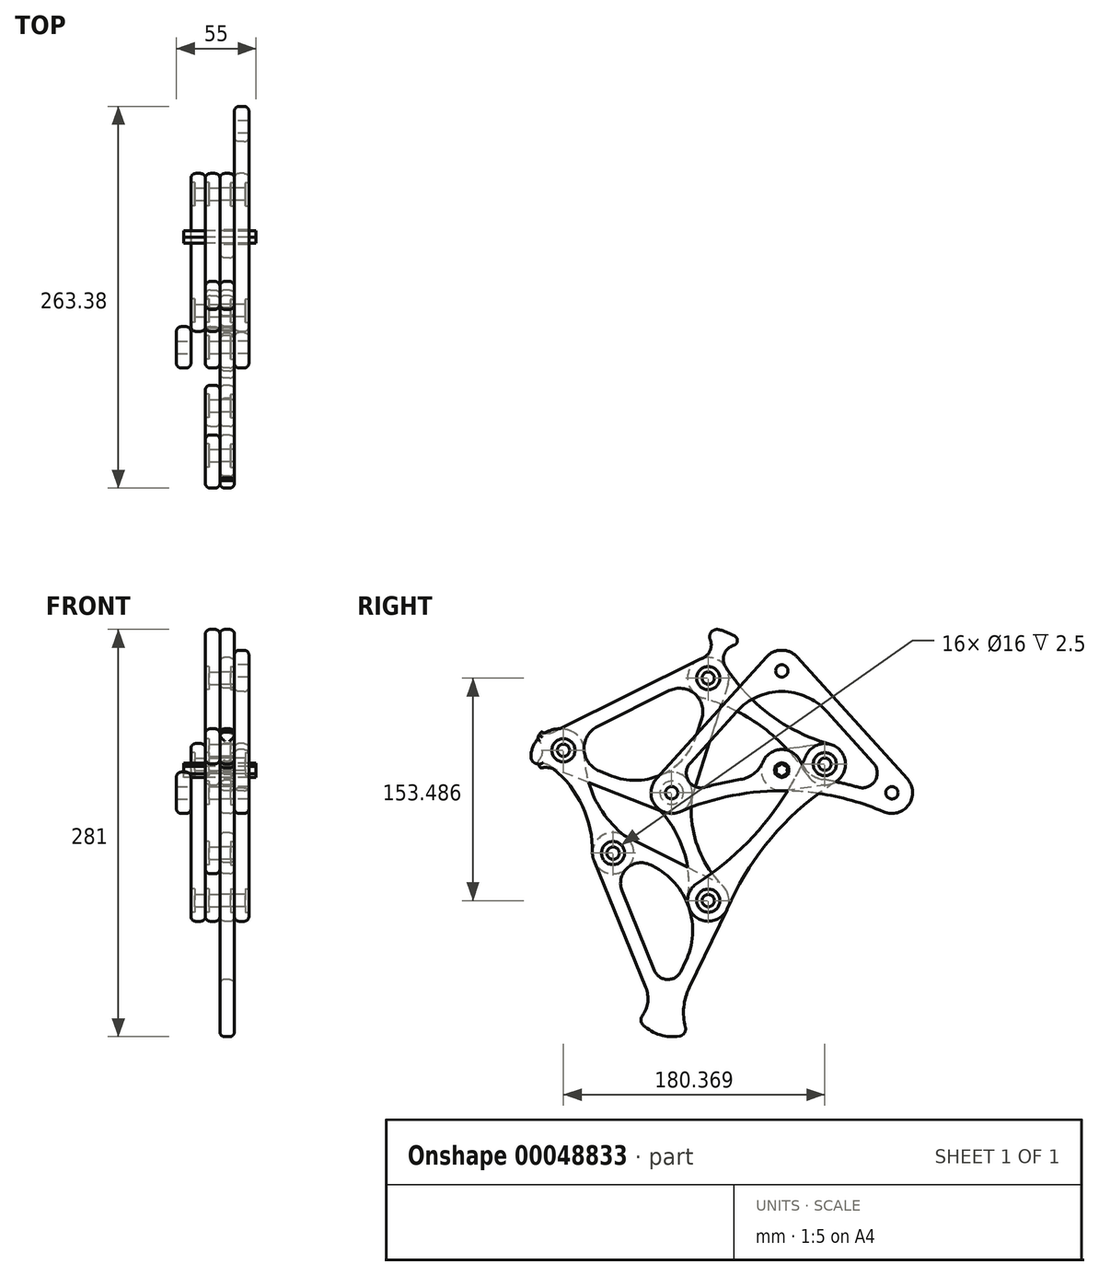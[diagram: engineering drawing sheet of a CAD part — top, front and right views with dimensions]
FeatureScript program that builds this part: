
annotation { "Feature Type Name" : "Feature", "Feature Type Description" : "" }
export const myFeature = defineFeature(function(context is Context, id is Id, definition is map)
    precondition{}
    {
        {
            assignVariable(context, id + "F0", {"name" : "WALL", "anyValue" : 10});
        }
        {
            var Q0;
            Q0=qCreatedBy(makeId("Right.planeOp"),FACE);
            var sketch = newSketch(context, id + "F1", { "sketchPlane" : qUnion([Q0])});
            skLineSegment(sketch, "E0", {"start": v(0, 0) * mm, "end": v(29.72, 4.1) * mm});
            skLineSegment(sketch, "E1", {"start": v(29.72, 4.1) * mm, "end": v(-50.75, 63.47) * mm});
            skLineSegment(sketch, "E2", {"start": v(-50.75, 63.47) * mm, "end": v(-76, -15.6) * mm});
            skLineSegment(sketch, "E3", {"start": v(-76, -15.6) * mm, "end": v(-50.7, -90.02) * mm});
            skLineSegment(sketch, "E4", {"start": v(-50.7, -90.02) * mm, "end": v(29.72, 4.1) * mm});
            skLineSegment(sketch, "E5", {"start": v(-76, -15.6) * mm, "end": v(-150.65, 13.72) * mm});
            skLineSegment(sketch, "E6", {"start": v(-150.65, 13.72) * mm, "end": v(-50.75, 63.47) * mm});
            skLineSegment(sketch, "E7", {"start": v(-50.7, -90.02) * mm, "end": v(-116.38, -57.24) * mm});
            skLineSegment(sketch, "E8", {"start": v(-116.38, -57.24) * mm, "end": v(-150.65, 13.72) * mm});
            skLineSegment(sketch, "E9", {"start": v(-116.38, -57.24) * mm, "end": v(-80.05, -183.52) * mm});
            skLineSegment(sketch, "E10", {"start": v(-80.05, -183.52) * mm, "end": v(-50.7, -90.02) * mm});
            skLineSegment(sketch, "E11", {"start": v(0, 0) * mm, "end": v(0, 67.08) * mm, "construction": true});
            skSolve(sketch);
        }
        {
            var Q0;
            Q0=qCreatedBy(makeId("Right.planeOp"),FACE);
            var sketch = newSketch(context, id + "F2", { "sketchPlane" : qUnion([Q0])});
            skLineSegment(sketch, "E12.rect.bottom", {"start": v(-228.6, 228.6) * mm, "end": v(228.6, 228.6) * mm, "construction": true});
            skLineSegment(sketch, "E12.rect.top", {"start": v(-228.6, -228.6) * mm, "end": v(228.6, -228.6) * mm, "construction": true});
            skLineSegment(sketch, "E12.rect.left", {"start": v(-228.6, 228.6) * mm, "end": v(-228.6, -228.6) * mm, "construction": true});
            skLineSegment(sketch, "E12.rect.right", {"start": v(228.6, 228.6) * mm, "end": v(228.6, -228.6) * mm, "construction": true});
            skPoint(sketch, "E12.rect.middle", {"position": v(0, 0) * mm});
            skSolve(sketch);
        }
        {
            var Q0;
            Q0=qCreatedBy(makeId("Right.planeOp"),FACE);
            var sketch = newSketch(context, id + "F3", { "sketchPlane" : qUnion([Q0])});
            skCircle(sketch, "E13.cCircle", {"center": v(0, 0) * mm, "radius": 6 * mm, "construction": true});
            skLineSegment(sketch, "E13.0", {"start": v(0, 6) * mm, "end": v(5.2, 3) * mm, "construction": true});
            skLineSegment(sketch, "E13.1", {"start": v(5.2, 3) * mm, "end": v(5.2, -3) * mm, "construction": true});
            skLineSegment(sketch, "E13.2", {"start": v(5.2, -3) * mm, "end": v(0, -6) * mm, "construction": true});
            skLineSegment(sketch, "E13.3", {"start": v(0, -6) * mm, "end": v(-5.2, -3) * mm, "construction": true});
            skLineSegment(sketch, "E13.4", {"start": v(-5.2, -3) * mm, "end": v(-5.2, 3) * mm, "construction": true});
            skLineSegment(sketch, "E13.5", {"start": v(-5.2, 3) * mm, "end": v(0, 6) * mm, "construction": true});
            skArc(sketch, "E14", {"start": v(-5.2, 3) * mm, "mid": v(-2.1, 3.63) * mm, "end": v(0, 6) * mm});
            skArc(sketch, "E15.1.0", {"start": v(-5.2, -3) * mm, "mid": v(-4.2, 0) * mm, "end": v(-5.2, 3) * mm});
            skArc(sketch, "E15.2.0", {"start": v(0, -6) * mm, "mid": v(-2.1, -3.63) * mm, "end": v(-5.2, -3) * mm});
            skArc(sketch, "E15.3.0", {"start": v(5.2, -3) * mm, "mid": v(2.1, -3.63) * mm, "end": v(0, -6) * mm});
            skArc(sketch, "E15.4.0", {"start": v(5.2, 3) * mm, "mid": v(4.2, 0) * mm, "end": v(5.2, -3) * mm});
            skArc(sketch, "E15.5.0", {"start": v(0, 6) * mm, "mid": v(2.1, 3.63) * mm, "end": v(5.2, 3) * mm});
            skArc(sketch, "E16.0", {"start": v(-4.28, -2.47) * mm, "mid": v(-3.7, 0) * mm, "end": v(-4.28, 2.47) * mm});
            skArc(sketch, "E16.1", {"start": v(0, 4.95) * mm, "mid": v(1.85, 3.2) * mm, "end": v(4.28, 2.47) * mm});
            skArc(sketch, "E16.2", {"start": v(4.28, 2.47) * mm, "mid": v(3.7, 0) * mm, "end": v(4.28, -2.47) * mm});
            skArc(sketch, "E16.3", {"start": v(-4.28, 2.47) * mm, "mid": v(-1.85, 3.2) * mm, "end": v(0, 4.95) * mm});
            skArc(sketch, "E16.4", {"start": v(4.28, -2.47) * mm, "mid": v(1.85, -3.2) * mm, "end": v(0, -4.95) * mm});
            skArc(sketch, "E16.5", {"start": v(0, -4.95) * mm, "mid": v(-1.85, -3.2) * mm, "end": v(-4.28, -2.47) * mm});
            skSolve(sketch);
        }
        {
            var Q0;
            Q0=qCreatedBy(makeId("Right.planeOp"),FACE);
            var sketch = newSketch(context, id + "F4", { "sketchPlane" : qUnion([Q0])});
            skPoint(sketch, "E17.0", {"position": v(-50.75, 63.47) * mm});
            skPoint(sketch, "E17.1", {"position": v(29.72, 4.1) * mm});
            skPoint(sketch, "E17.2", {"position": v(-150.65, 13.72) * mm});
            skPoint(sketch, "E17.3", {"position": v(-76, -15.6) * mm});
            skPoint(sketch, "E17.4", {"position": v(-116.38, -57.24) * mm});
            skPoint(sketch, "E17.5", {"position": v(-50.7, -90.02) * mm});
            skPoint(sketch, "E17.6", {"position": v(0, 0) * mm});
            skCircle(sketch, "E18", {"center": v(-50.75, 63.47) * mm, "radius": 4.25 * mm});
            skCircle(sketch, "E19", {"center": v(-150.65, 13.72) * mm, "radius": 4.25 * mm});
            skCircle(sketch, "E20", {"center": v(-76, -15.6) * mm, "radius": 4.25 * mm});
            skCircle(sketch, "E21", {"center": v(-116.38, -57.24) * mm, "radius": 4.25 * mm});
            skCircle(sketch, "E22", {"center": v(-50.7, -90.02) * mm, "radius": 4.25 * mm});
            skCircle(sketch, "E23", {"center": v(29.72, 4.1) * mm, "radius": 4.25 * mm});
            skCircle(sketch, "E24", {"center": v(0, 0) * mm, "radius": 4.25 * mm});
            skCircle(sketch, "E25", {"center": v(-50.75, 63.47) * mm, "radius": 14.25 * mm});
            skCircle(sketch, "E26", {"center": v(-150.65, 13.72) * mm, "radius": 14.25 * mm});
            skCircle(sketch, "E27", {"center": v(-76, -15.6) * mm, "radius": 14.25 * mm});
            skCircle(sketch, "E28", {"center": v(0, 0) * mm, "radius": 14.25 * mm});
            skCircle(sketch, "E29", {"center": v(29.72, 4.1) * mm, "radius": 14.25 * mm});
            skCircle(sketch, "E30", {"center": v(-116.38, -57.24) * mm, "radius": 14.25 * mm});
            skCircle(sketch, "E31", {"center": v(-50.7, -90.02) * mm, "radius": 14.25 * mm});
            skSolve(sketch);
        }
        {
            var Q0;
            Q0=qCreatedBy(makeId("Right.planeOp"),FACE);
            var sketch = newSketch(context, id + "F5", { "sketchPlane" : qUnion([Q0])});
            skLineSegment(sketch, "E32", {"start": v(-157, 26.47) * mm, "end": v(-57.1, 76.22) * mm});
            skLineSegment(sketch, "E33", {"start": v(-37.18, 59.13) * mm, "end": v(-62.43, -19.93) * mm});
            skLineSegment(sketch, "E34", {"start": v(-81.2, -28.86) * mm, "end": v(-155.86, 0.45) * mm});
            skArc(sketch, "E35", {"start": v(-157, 26.47) * mm, "mid": v(-164.89, 13.09) * mm, "end": v(-155.86, 0.45) * mm});
            skArc(sketch, "E36", {"start": v(-81.2, -28.86) * mm, "mid": v(-69.88, -28.47) * mm, "end": v(-62.43, -19.93) * mm});
            skArc(sketch, "E37", {"start": v(-37.18, 59.13) * mm, "mid": v(-41.48, 74.28) * mm, "end": v(-57.1, 76.22) * mm});
            skCircle(sketch, "E38.0", {"center": v(-150.65, 13.72) * mm, "radius": 4.25 * mm});
            skCircle(sketch, "E38.1", {"center": v(-50.75, 63.47) * mm, "radius": 4.25 * mm});
            skCircle(sketch, "E38.2", {"center": v(-76, -15.6) * mm, "radius": 4.25 * mm});
            skLineSegment(sketch, "E39", {"start": v(-127.07, 30.2) * mm, "end": v(-77.62, 54.83) * mm});
            skLineSegment(sketch, "E40", {"start": v(-55.2, 35.6) * mm, "end": v(-58.97, 23.77) * mm});
            skLineSegment(sketch, "E41", {"start": v(-117.28, -3.95) * mm, "end": v(-125.7, -0.65) * mm});
            skPoint(sketch, "E42.visualSharp", {"position": v(-161.1, 13.26) * mm});
            skArc(sketch, "E42.filletArc", {"start": v(-127.07, 30.2) * mm, "mid": v(-136.41, 14.34) * mm, "end": v(-125.7, -0.65) * mm});
            skPoint(sketch, "E43.visualSharp", {"position": v(-43.65, 71.75) * mm});
            skArc(sketch, "E43.filletArc", {"start": v(-55.2, 35.6) * mm, "mid": v(-60.03, 52.65) * mm, "end": v(-77.62, 54.83) * mm});
            skPoint(sketch, "E44.visualSharp", {"position": v(-73.33, -21.21) * mm});
            skArc(sketch, "E44.filletArc", {"start": v(-117.28, -3.95) * mm, "mid": v(-82.12, -2.73) * mm, "end": v(-58.97, 23.77) * mm});
            skLineSegment(sketch, "E45", {"start": v(-129.57, -62.64) * mm, "end": v(-80.05, -183.52) * mm});
            skLineSegment(sketch, "E46", {"start": v(-110.02, -44.5) * mm, "end": v(-44.34, -77.27) * mm});
            skLineSegment(sketch, "E47", {"start": v(-37.87, -96.22) * mm, "end": v(-80.05, -183.52) * mm});
            skArc(sketch, "E48", {"start": v(-110.02, -44.5) * mm, "mid": v(-126.08, -46.8) * mm, "end": v(-129.57, -62.64) * mm});
            skArc(sketch, "E49", {"start": v(-37.87, -96.22) * mm, "mid": v(-37.22, -85.42) * mm, "end": v(-44.34, -77.27) * mm});
            skLineSegment(sketch, "E50", {"start": v(-87.8, -138.22) * mm, "end": v(-110.19, -83.58) * mm});
            skLineSegment(sketch, "E51", {"start": v(-90.58, -65.37) * mm, "end": v(-89.14, -66.09) * mm});
            skLineSegment(sketch, "E52", {"start": v(-66.48, -132.45) * mm, "end": v(-69.54, -138.78) * mm});
            skPoint(sketch, "E53.visualSharp", {"position": v(-124.6, -48.4) * mm});
            skArc(sketch, "E53.filletArc", {"start": v(-90.58, -65.37) * mm, "mid": v(-106.68, -67.69) * mm, "end": v(-110.19, -83.58) * mm});
            skPoint(sketch, "E54.visualSharp", {"position": v(-45.05, -88.09) * mm});
            skArc(sketch, "E54.filletArc", {"start": v(-66.48, -132.45) * mm, "mid": v(-64.2, -94.62) * mm, "end": v(-89.14, -66.09) * mm});
            skPoint(sketch, "E55.visualSharp", {"position": v(-79.3, -158.98) * mm});
            skArc(sketch, "E55.filletArc", {"start": v(-87.8, -138.22) * mm, "mid": v(-78.85, -144.43) * mm, "end": v(-69.54, -138.78) * mm});
            skCircle(sketch, "E56.0", {"center": v(-116.38, -57.24) * mm, "radius": 4.25 * mm});
            skCircle(sketch, "E56.1", {"center": v(-50.7, -90.02) * mm, "radius": 4.25 * mm});
            skLineSegment(sketch, "E57", {"start": v(-1.95, 14.12) * mm, "end": v(27.77, 18.22) * mm});
            skLineSegment(sketch, "E58", {"start": v(31.67, -10.01) * mm, "end": v(1.95, -14.12) * mm});
            skArc(sketch, "E59", {"start": v(-1.95, 14.12) * mm, "mid": v(-14.12, -1.95) * mm, "end": v(1.95, -14.12) * mm});
            skArc(sketch, "E60", {"start": v(31.67, -10.01) * mm, "mid": v(43.83, 6.05) * mm, "end": v(27.77, 18.22) * mm});
            skCircle(sketch, "E61.0", {"center": v(0, 0) * mm, "radius": 4.25 * mm, "construction": true});
            skCircle(sketch, "E61.1", {"center": v(29.72, 4.1) * mm, "radius": 4.25 * mm});
            skArc(sketch, "E62", {"start": v(-96.23, -169.37) * mm, "mid": v(-92.48, -159.96) * mm, "end": v(-93.82, -149.92) * mm});
            skArc(sketch, "E63", {"start": v(-63.82, -149.92) * mm, "mid": v(-67.6, -163.38) * mm, "end": v(-66.53, -177.33) * mm});
            skArc(sketch, "E64", {"start": v(-95.58, -176.02) * mm, "mid": v(-83.94, -182.63) * mm, "end": v(-70.58, -183.52) * mm});
            skPoint(sketch, "E65.visualSharp", {"position": v(-98.95, -172.37) * mm});
            skArc(sketch, "E65.filletArc", {"start": v(-96.23, -169.37) * mm, "mid": v(-97.18, -172.82) * mm, "end": v(-95.58, -176.02) * mm});
            skPoint(sketch, "E66.visualSharp", {"position": v(-64.98, -182.06) * mm});
            skArc(sketch, "E66.filletArc", {"start": v(-70.58, -183.52) * mm, "mid": v(-67.18, -181.32) * mm, "end": v(-66.53, -177.33) * mm});
            skArc(sketch, "E67", {"start": v(-165.92, 26.47) * mm, "mid": v(-161.46, 25.42) * mm, "end": v(-157, 26.47) * mm});
            skArc(sketch, "E68", {"start": v(-155.86, 0.45) * mm, "mid": v(-161.06, 1.72) * mm, "end": v(-166.4, 1.57) * mm});
            skArc(sketch, "E69", {"start": v(-165.92, 26.47) * mm, "mid": v(-170.54, 14.1) * mm, "end": v(-166.4, 1.57) * mm});
            skArc(sketch, "E70", {"start": v(-168.87, 5.73) * mm, "mid": v(-164.9, 13.72) * mm, "end": v(-168.87, 21.7) * mm});
            skArc(sketch, "E71.0", {"start": v(-5.2, 3) * mm, "mid": v(-2.1, 3.63) * mm, "end": v(0, 6) * mm});
            skArc(sketch, "E71.1", {"start": v(-5.2, -3) * mm, "mid": v(-4.2, 0) * mm, "end": v(-5.2, 3) * mm});
            skArc(sketch, "E71.2", {"start": v(0, -6) * mm, "mid": v(-2.1, -3.63) * mm, "end": v(-5.2, -3) * mm});
            skArc(sketch, "E71.3", {"start": v(5.2, -3) * mm, "mid": v(2.1, -3.63) * mm, "end": v(0, -6) * mm});
            skArc(sketch, "E71.4", {"start": v(5.2, 3) * mm, "mid": v(4.2, 0) * mm, "end": v(5.2, -3) * mm});
            skArc(sketch, "E71.5", {"start": v(0, 6) * mm, "mid": v(2.1, 3.63) * mm, "end": v(5.2, 3) * mm});
            skSolve(sketch);
        }
        {
            var Q0;
            Q0=qCreatedBy(makeId("Right.planeOp"),FACE);
            var sketch = newSketch(context, id + "F6", { "sketchPlane" : qUnion([Q0])});
            skArc(sketch, "E72", {"start": v(-136.4, 13.55) * mm, "mid": v(-156.85, 26.55) * mm, "end": v(-159.38, 2.46) * mm});
            skArc(sketch, "E73", {"start": v(-130.63, -57.08) * mm, "mid": v(-110.18, -70.07) * mm, "end": v(-107.65, -45.98) * mm});
            skLineSegment(sketch, "E74", {"start": v(-150.65, 13.72) * mm, "end": v(-116.38, -57.24) * mm, "construction": true});
            skLineSegment(sketch, "E75", {"start": v(-204.91, -56.24) * mm, "end": v(-62.12, 12.72) * mm, "construction": true});
            skPoint(sketch, "E76", {"position": v(-133.52, -21.76) * mm});
            skArc(sketch, "E77", {"start": v(-130.63, -57.08) * mm, "mid": v(-138.02, -23.94) * mm, "end": v(-159.38, 2.46) * mm});
            skArc(sketch, "E78.MirrorCS", {"start": v(-107.65, -45.98) * mm, "mid": v(-129.01, -19.59) * mm, "end": v(-136.4, 13.55) * mm});
            skCircle(sketch, "E79.0", {"center": v(-150.65, 13.72) * mm, "radius": 4.25 * mm});
            skCircle(sketch, "E79.1", {"center": v(-116.38, -57.24) * mm, "radius": 4.25 * mm});
            skArc(sketch, "E80", {"start": v(-61.88, -17.51) * mm, "mid": v(-80.59, -2.1) * mm, "end": v(-86.03, -25.72) * mm});
            skArc(sketch, "E81", {"start": v(-64.83, -88.1) * mm, "mid": v(-68.09, -54.42) * mm, "end": v(-86.03, -25.72) * mm});
            skArc(sketch, "E82.MirrorCS", {"start": v(-40.67, -79.9) * mm, "mid": v(-58.62, -51.2) * mm, "end": v(-61.88, -17.51) * mm});
            skArc(sketch, "E83", {"start": v(-64.83, -88.1) * mm, "mid": v(-46.12, -103.51) * mm, "end": v(-40.67, -79.9) * mm});
            skLineSegment(sketch, "E84", {"start": v(-138.02, -78.19) * mm, "end": v(11.31, -27.43) * mm, "construction": true});
            skLineSegment(sketch, "E85", {"start": v(-76, -15.6) * mm, "end": v(-50.7, -90.02) * mm, "construction": true});
            skCircle(sketch, "E86.0", {"center": v(-76, -15.6) * mm, "radius": 4.25 * mm});
            skCircle(sketch, "E87.1", {"center": v(-50.7, -90.02) * mm, "radius": 4.25 * mm});
            skArc(sketch, "E88", {"start": v(-38.75, 71.15) * mm, "mid": v(-62.22, 71.93) * mm, "end": v(-54.55, 49.73) * mm});
            skArc(sketch, "E89", {"start": v(17.72, -3.58) * mm, "mid": v(-13.49, 29.76) * mm, "end": v(-54.55, 49.73) * mm});
            skArc(sketch, "E90.MirrorCS", {"start": v(33.52, 17.84) * mm, "mid": v(-7.55, 37.8) * mm, "end": v(-38.75, 71.15) * mm});
            skArc(sketch, "E91", {"start": v(17.72, -3.58) * mm, "mid": v(41.19, -4.36) * mm, "end": v(33.52, 17.84) * mm});
            skLineSegment(sketch, "E92", {"start": v(-88, -71.24) * mm, "end": v(66.96, 138.8) * mm, "construction": true});
            skLineSegment(sketch, "E93", {"start": v(-50.75, 63.47) * mm, "end": v(29.72, 4.1) * mm, "construction": true});
            skArc(sketch, "E94", {"start": v(-159.38, 2.46) * mm, "mid": v(-163.11, 4.26) * mm, "end": v(-167.26, 4.4) * mm});
            skArc(sketch, "E95", {"start": v(-144.45, 26.55) * mm, "mid": v(-163.33, 25.75) * mm, "end": v(-173.12, 9.58) * mm});
            skPoint(sketch, "E96", {"position": v(-156.85, 26.55) * mm});
            skPoint(sketch, "E97.visualSharp", {"position": v(-172.08, 2.1) * mm});
            skArc(sketch, "E97.filletArc", {"start": v(-173.12, 9.58) * mm, "mid": v(-171.44, 5.58) * mm, "end": v(-167.26, 4.4) * mm});
            skArc(sketch, "E98", {"start": v(-55.4, 76.94) * mm, "mid": v(-49.55, 82.28) * mm, "end": v(-49.42, 90.2) * mm});
            skArc(sketch, "E99", {"start": v(-33.01, 86.17) * mm, "mid": v(-39.67, 80.1) * mm, "end": v(-38.75, 71.15) * mm});
            skArc(sketch, "E100", {"start": v(-32.1, 92.18) * mm, "mid": v(-37.7, 95.13) * mm, "end": v(-43.77, 97) * mm});
            skPoint(sketch, "E101.visualSharp", {"position": v(-61.5, 95.98) * mm});
            skArc(sketch, "E101.filletArc", {"start": v(-43.77, 97) * mm, "mid": v(-48.64, 95.29) * mm, "end": v(-49.42, 90.2) * mm});
            skPoint(sketch, "E102.visualSharp", {"position": v(-22.16, 82.3) * mm});
            skArc(sketch, "E102.filletArc", {"start": v(-33.01, 86.17) * mm, "mid": v(-30.61, 88.88) * mm, "end": v(-32.1, 92.18) * mm});
            skCircle(sketch, "E103.0", {"center": v(-50.75, 63.47) * mm, "radius": 4.25 * mm});
            skCircle(sketch, "E103.1", {"center": v(29.72, 4.1) * mm, "radius": 4.25 * mm});
            skSolve(sketch);
        }
        {
            var Q0;
            Q0=qCreatedBy(makeId("Right.planeOp"),FACE);
            var sketch = newSketch(context, id + "F7", { "sketchPlane" : qUnion([Q0])});
            skCircle(sketch, "E104.0", {"center": v(-50.7, -90.02) * mm, "radius": 4.25 * mm});
            skCircle(sketch, "E104.1", {"center": v(29.72, 4.1) * mm, "radius": 4.25 * mm});
            skArc(sketch, "E105", {"start": v(-58.36, -78) * mm, "mid": v(-59.96, -100.85) * mm, "end": v(-37.64, -95.7) * mm});
            skArc(sketch, "E106", {"start": v(37.37, -7.92) * mm, "mid": v(38.98, 14.94) * mm, "end": v(16.65, 9.79) * mm});
            skLineSegment(sketch, "E107", {"start": v(-50.7, -90.02) * mm, "end": v(29.72, 4.1) * mm, "construction": true});
            skLineSegment(sketch, "E108", {"start": v(-164.44, 88.58) * mm, "end": v(143.45, -174.5) * mm, "construction": true});
            skPoint(sketch, "E109", {"position": v(-10.5, -42.96) * mm});
            skArc(sketch, "E110", {"start": v(-58.36, -78) * mm, "mid": v(-14.3, -39.71) * mm, "end": v(16.65, 9.79) * mm});
            skArc(sketch, "E111", {"start": v(37.37, -7.92) * mm, "mid": v(-6.7, -46.2) * mm, "end": v(-37.64, -95.7) * mm});
            skSolve(sketch);
        }
        {
            var Q0;
            Q0=qCreatedBy(makeId("Right.planeOp"),FACE);
            var sketch = newSketch(context, id + "F8", { "sketchPlane" : qUnion([Q0])});
            skCircle(sketch, "E112.0", {"center": v(-76, -15.6) * mm, "radius": 4.25 * mm});
            skLineSegment(sketch, "E113", {"start": v(-86.57, -6.05) * mm, "end": v(-10.57, 78.05) * mm});
            skCircle(sketch, "E114", {"center": v(0, 68.5) * mm, "radius": 4.25 * mm});
            skArc(sketch, "E115", {"start": v(10.57, 78.05) * mm, "mid": v(0, 82.75) * mm, "end": v(-10.57, 78.05) * mm});
            skCircle(sketch, "E116", {"center": v(0, 0) * mm, "radius": 44.25 * mm, "construction": true});
            skCircle(sketch, "E117.MirrorC", {"center": v(-97.15, 3.5) * mm, "radius": 4.25 * mm});
            skLineSegment(sketch, "E118", {"start": v(0, 0) * mm, "end": v(0, 68.5) * mm, "construction": true});
            skCircle(sketch, "E119.MirrorC", {"center": v(76, -15.6) * mm, "radius": 4.25 * mm});
            skLineSegment(sketch, "E120.MirrorCS", {"start": v(86.57, -6.05) * mm, "end": v(10.57, 78.05) * mm});
            skArc(sketch, "E121", {"start": v(70.39, -28.7) * mm, "mid": v(0, -14.25) * mm, "end": v(-70.39, -28.7) * mm});
            skArc(sketch, "E122", {"start": v(-86.57, -6.05) * mm, "mid": v(-87.6, -23.88) * mm, "end": v(-70.39, -28.7) * mm});
            skArc(sketch, "E123.MirrorCS", {"start": v(86.57, -6.05) * mm, "mid": v(87.6, -23.88) * mm, "end": v(70.39, -28.7) * mm});
            skLineSegment(sketch, "E124", {"start": v(31.08, 40.45) * mm, "end": v(63.25, 4.85) * mm});
            skLineSegment(sketch, "E125", {"start": v(-31.08, 40.45) * mm, "end": v(-63.25, 4.85) * mm});
            skArc(sketch, "E126", {"start": v(52.82, -11.8) * mm, "mid": v(0, -4.25) * mm, "end": v(-52.82, -11.8) * mm});
            skArc(sketch, "E127", {"start": v(13.44, -4.73) * mm, "mid": v(0, 14.25) * mm, "end": v(-13.44, -4.73) * mm});
            skPoint(sketch, "E128.visualSharp", {"position": v(-94.29, -29.5) * mm});
            skArc(sketch, "E128.filletArc", {"start": v(-63.25, 4.85) * mm, "mid": v(-64.33, -7.42) * mm, "end": v(-52.82, -11.8) * mm});
            skPoint(sketch, "E129.visualSharp", {"position": v(0, 74.84) * mm});
            skArc(sketch, "E129.filletArc", {"start": v(31.08, 40.45) * mm, "mid": v(0, 54.25) * mm, "end": v(-31.08, 40.45) * mm});
            skPoint(sketch, "E130.visualSharp", {"position": v(94.29, -29.5) * mm});
            skArc(sketch, "E130.filletArc", {"start": v(52.82, -11.8) * mm, "mid": v(64.33, -7.42) * mm, "end": v(63.25, 4.85) * mm});
            skArc(sketch, "E131", {"start": v(-28.52, -6.42) * mm, "mid": v(-19.26, -2.43) * mm, "end": v(-13.12, 5.56) * mm});
            skArc(sketch, "E132", {"start": v(13.12, 5.56) * mm, "mid": v(19.26, -2.43) * mm, "end": v(28.52, -6.42) * mm});
            skCircle(sketch, "E133.0", {"center": v(0, 0) * mm, "radius": 6 * mm, "construction": true});
            skCircle(sketch, "E134", {"center": v(0, 0) * mm, "radius": 4.95 * mm});
            skSolve(sketch);
        }
        {
            var Q0;
            Q0=makeQuery(id+"F4.imprint","IMPRINT",FACE,{"disambiguationData":[TD([[makeQuery(id+"F4.imprint","IMPRINT",EDGE,{"derivedFrom":sQuery(id+"F4.wireOp",EDGE,"E20")}),-1.0]])]});
            extrude(context, id + "F9", {"entities" : qUnion([Q0]), "oppositeDirection" : true, "depth" : (getVariable(context, 'WALL') * 3) * mm, "hasSecondDirection" : true, "secondDirectionOppositeDirection" : true, "secondDirectionDepth" : (getVariable(context, 'WALL') * 2) * mm});
        }
        {
            var Q0;
            Q0=makeQuery(id+"F3.imprint","IMPRINT",FACE,{"disambiguationData":[TD([[makeQuery(id+"F3.imprint","IMPRINT",EDGE,{"derivedFrom":sQuery(id+"F3.wireOp",EDGE,"E16.0")}),-1.0]])]});
            extrude(context, id + "F10", {"entities" : qUnion([Q0]), "depth" : 50 * mm, "symmetric" : true});
        }
        {
            var Q0;
            {var subQ2=sQuery(id+"F5.wireOp",EDGE,"E32");Q0=makeQuery(id+"F5.imprint","IMPRINT",FACE,{"disambiguationData":[TD([[makeQuery(id+"F5.imprint","IMPRINT",EDGE,{"derivedFrom":subQ2}),-1.0]])]});}
            var Q1;
            {var subQ5=sQuery(id+"F5.wireOp",EDGE,"E67");Q1=makeQuery(id+"F5.imprint","IMPRINT",FACE,{"disambiguationData":[TD([[makeQuery(id+"F5.imprint","IMPRINT",EDGE,{"derivedFrom":subQ5}),-1.0]])]});}
            var Q2;
            {var subQ5=sQuery(id+"F5.wireOp",EDGE,"E68");Q2=makeQuery(id+"F5.imprint","IMPRINT",FACE,{"disambiguationData":[TD([[makeQuery(id+"F5.imprint","IMPRINT",EDGE,{"derivedFrom":subQ5}),-1.0]])]});}
            var Q3;
            Q3=makeQuery(id+"F5.imprint","IMPRINT",FACE,{"disambiguationData":[TD([[makeQuery(id+"F5.imprint","IMPRINT",EDGE,{"derivedFrom":sQuery(id+"F5.wireOp",EDGE,"E46")}),-1.0]])]});
            var Q4;
            {var subQ4=sQuery(id+"F5.wireOp",EDGE,"E62");Q4=makeQuery(id+"F5.imprint","IMPRINT",FACE,{"disambiguationData":[TD([[makeQuery(id+"F5.imprint","IMPRINT",EDGE,{"derivedFrom":subQ4}),-1.0]])]});}
            var Q5;
            {var subQ4=sQuery(id+"F5.wireOp",EDGE,"E63");Q5=makeQuery(id+"F5.imprint","IMPRINT",FACE,{"disambiguationData":[TD([[makeQuery(id+"F5.imprint","IMPRINT",EDGE,{"derivedFrom":subQ4}),-1.0]])]});}
            extrude(context, id + "F11", {"entities" : qUnion([Q0, Q1, Q2, Q3, Q4, Q5]), "depth" : (getVariable(context, 'WALL')) * mm});
        }
        {
            var Q0;
            Q0=makeQuery(id+"F5.imprint","IMPRINT",FACE,{"disambiguationData":[TD([[makeQuery(id+"F5.imprint","IMPRINT",EDGE,{"derivedFrom":sQuery(id+"F5.wireOp",EDGE,"E57")}),-1.0]])]});
            extrude(context, id + "F12", {"entities" : qUnion([Q0]), "depth" : (getVariable(context, 'WALL')) * mm});
        }
        {
            var Q0;
            Q0=makeQuery(id+"F6.imprint","IMPRINT",FACE,{"disambiguationData":[TD([[makeQuery(id+"F6.imprint","IMPRINT",EDGE,{"derivedFrom":sQuery(id+"F6.wireOp",EDGE,"E73")}),1.0]])]});
            var Q1;
            {var subQ1=sQuery(id+"F6.wireOp",EDGE,"E94");Q1=makeQuery(id+"F6.imprint","IMPRINT",FACE,{"disambiguationData":[TD([[makeQuery(id+"F6.imprint","IMPRINT",EDGE,{"derivedFrom":subQ1}),-1.0]])]});}
            var Q2;
            Q2=makeQuery(id+"F6.imprint","IMPRINT",FACE,{"disambiguationData":[TD([[makeQuery(id+"F6.imprint","IMPRINT",EDGE,{"derivedFrom":sQuery(id+"F6.wireOp",EDGE,"E80")}),1.0]])]});
            var Q3;
            {var subQ3=sQuery(id+"F6.wireOp",EDGE,"E89");Q3=makeQuery(id+"F6.imprint","IMPRINT",FACE,{"disambiguationData":[TD([[makeQuery(id+"F6.imprint","IMPRINT",EDGE,{"derivedFrom":subQ3}),-1.0]])]});}
            var Q4;
            {var subQ1=sQuery(id+"F6.wireOp",EDGE,"E98");Q4=makeQuery(id+"F6.imprint","IMPRINT",FACE,{"disambiguationData":[TD([[makeQuery(id+"F6.imprint","IMPRINT",EDGE,{"derivedFrom":subQ1}),-1.0]])]});}
            extrude(context, id + "F13", {"entities" : qUnion([Q0, Q1, Q2, Q3, Q4]), "oppositeDirection" : true, "depth" : (getVariable(context, 'WALL')) * mm});
        }
        {
            var Q0;
            Q0=makeQuery(id+"F7.imprint","IMPRINT",FACE,{"disambiguationData":[TD([[makeQuery(id+"F7.imprint","IMPRINT",EDGE,{"derivedFrom":sQuery(id+"F7.wireOp",EDGE,"E104.0")}),-1.0]])]});
            extrude(context, id + "F14", {"entities" : qUnion([Q0]), "oppositeDirection" : true, "depth" : (getVariable(context, 'WALL') * 2) * mm, "hasSecondDirection" : true, "secondDirectionOppositeDirection" : true, "secondDirectionDepth" : (getVariable(context, 'WALL')) * mm});
        }
        {
            var Q0;
            Q0=makeQuery(id+"F8.imprint","IMPRINT",FACE,{"disambiguationData":[TD([[makeQuery(id+"F8.imprint","IMPRINT",EDGE,{"derivedFrom":sQuery(id+"F8.wireOp",EDGE,"E112.0")}),-1.0]])]});
            var Q1;
            {var subQ1=sQuery(id+"F8.wireOp",EDGE,"E126");var subQ4=sQuery(id+"F8.wireOp",EDGE,"E127");var subQ7=makeQuery(id+"F8.imprint","INTERSECT",VERTEX,{"disambiguationData":[OD(0.0)],"derivedFrom":[subQ1,subQ4]});Q1=makeQuery(id+"F8.imprint","IMPRINT",FACE,{"disambiguationData":[TD([[makeQuery(id+"F8.imprint","IMPRINT",EDGE,{"disambiguationData":[TD([[subQ7,-1.0]])],"derivedFrom":subQ1}),-1.0]])]});}
            var Q2;
            {var subQ0=sQuery(id+"F8.wireOp",EDGE,"E131");Q2=makeQuery(id+"F8.imprint","IMPRINT",FACE,{"disambiguationData":[TD([[makeQuery(id+"F8.imprint","IMPRINT",EDGE,{"derivedFrom":subQ0}),-1.0]])]});}
            var Q3;
            {var subQ0=sQuery(id+"F8.wireOp",EDGE,"E132");Q3=makeQuery(id+"F8.imprint","IMPRINT",FACE,{"disambiguationData":[TD([[makeQuery(id+"F8.imprint","IMPRINT",EDGE,{"derivedFrom":subQ0}),-1.0]])]});}
            extrude(context, id + "F15", {"entities" : qUnion([Q0, Q1, Q2, Q3]), "depth" : (getVariable(context, 'WALL') * 2) * mm, "hasSecondDirection" : true, "secondDirectionOppositeDirection" : false, "secondDirectionDepth" : (getVariable(context, 'WALL')) * mm});
        }
        {
            var Q0;
            Q0=makeQuery(id+"F13.opExtrude","SWEPT_FACE",FACE,{"disambiguationData":[OSD([sQuery(id+"F6.wireOp",EDGE,"E95")])]});
            var Q1;
            Q1=makeQuery(id+"F13.opExtrude","SWEPT_FACE",FACE,{"disambiguationData":[OSD([sQuery(id+"F6.wireOp",EDGE,"E88")])]});
            var Q2;
            Q2=makeQuery(id+"F13.opExtrude","SWEPT_FACE",FACE,{"disambiguationData":[OSD([sQuery(id+"F6.wireOp",EDGE,"E80")])]});
            var Q3;
            Q3=makeQuery(id+"F15.opExtrude","SWEPT_FACE",FACE,{"disambiguationData":[OSD([sQuery(id+"F8.wireOp",EDGE,"E113")])]});
            var Q4;
            Q4=makeQuery(id+"F15.opExtrude","SWEPT_FACE",FACE,{"disambiguationData":[OSD([sQuery(id+"F8.wireOp",EDGE,"E129.filletArc")])]});
            var Q5;
            Q5=makeQuery(id+"F14.opExtrude","SWEPT_FACE",FACE,{"disambiguationData":[OSD([sQuery(id+"F7.wireOp",EDGE,"E106")])]});
            var Q6;
            Q6=makeQuery(id+"F11.opExtrude","SWEPT_FACE",FACE,{"disambiguationData":[OSD([sQuery(id+"F5.wireOp",EDGE,"E32")])]});
            var Q7;
            Q7=makeQuery(id+"F11.opExtrude","SWEPT_FACE",FACE,{"disambiguationData":[OSD([sQuery(id+"F5.wireOp",EDGE,"E42.filletArc")])]});
            var Q8;
            Q8=makeQuery(id+"F11.opExtrude","SWEPT_FACE",FACE,{"disambiguationData":[OSD([sQuery(id+"F5.wireOp",EDGE,"E53.filletArc")])]});
            var Q9;
            Q9=makeQuery(id+"F11.opExtrude","SWEPT_FACE",FACE,{"disambiguationData":[OSD([sQuery(id+"F5.wireOp",EDGE,"E45")])]});
            var Q10;
            Q10=makeQuery(id+"F11.opExtrude","SWEPT_FACE",FACE,{"disambiguationData":[OSD([sQuery(id+"F5.wireOp",EDGE,"E70")])]});
            var Q11;
            Q11=makeQuery(id+"F11.opExtrude","SWEPT_FACE",FACE,{"disambiguationData":[OSD([sQuery(id+"F5.wireOp",EDGE,"E57")])]});
            var Q12;
            Q12=makeQuery(id+"F9.opExtrude","SWEPT_FACE",FACE,{"disambiguationData":[OSD([sQuery(id+"F4.wireOp",EDGE,"E27")])]});
            var Q13;
            Q13=makeQuery(id+"F12.opExtrude","SWEPT_FACE",FACE,{"disambiguationData":[OSD([sQuery(id+"F5.wireOp",EDGE,"E59")])]});
            fillet(context, id + "F16", {"entities" : qUnion([Q0, Q1, Q2, Q3, Q4, Q5, Q6, Q7, Q8, Q9, Q10, Q11, Q12, Q13]), "radius" : (getVariable(context, 'WALL') / 3) * mm, "tangentPropagation" : true, "allowEdgeOverflow" : false});
        }
        {
            var Q0;
            Q0=makeQuery(id+"F13.opExtrude","CAP_FACE",FACE,{"disambiguationData":[OSD([sQuery(id+"F6.wireOp",EDGE,"E72"),sQuery(id+"F6.wireOp",EDGE,"E73"),sQuery(id+"F6.wireOp",EDGE,"E77"),sQuery(id+"F6.wireOp",EDGE,"E78.MirrorCS"),sQuery(id+"F6.wireOp",EDGE,"E79.0"),sQuery(id+"F6.wireOp",EDGE,"E79.1"),sQuery(id+"F6.wireOp",EDGE,"E94"),sQuery(id+"F6.wireOp",EDGE,"E95"),sQuery(id+"F6.wireOp",EDGE,"E97.filletArc")])],"isStart":false});
            var sketch = newSketch(context, id + "F17", { "sketchPlane" : qUnion([Q0])});
            skCircle(sketch, "E135", {"center": v(150.65, 13.72) * mm, "radius": 8 * mm});
            skCircle(sketch, "E136", {"center": v(116.38, -57.24) * mm, "radius": 8 * mm});
            skSolve(sketch);
        }
        {
            var Q0;
            Q0=makeQuery(id+"F17.imprint","IMPRINT",FACE,{"disambiguationData":[TD([[makeQuery(id+"F17.imprint","IMPRINT",EDGE,{"derivedFrom":sQuery(id+"F17.wireOp",EDGE,"E135")}),1.0]])]});
            var Q1;
            Q1=makeQuery(id+"F17.imprint","IMPRINT",FACE,{"disambiguationData":[TD([[makeQuery(id+"F17.imprint","IMPRINT",EDGE,{"derivedFrom":sQuery(id+"F17.wireOp",EDGE,"E136")}),1.0]])]});
            extrude(context, id + "F18", {"entities" : qUnion([Q0, Q1]), "operationType" : NewBodyOperationType.REMOVE, "oppositeDirection" : true, "depth" : 2.5 * mm});
        }
        {
            var Q0;
            Q0=makeQuery(id+"F13.opExtrude","CAP_FACE",FACE,{"disambiguationData":[OSD([sQuery(id+"F6.wireOp",EDGE,"E80"),sQuery(id+"F6.wireOp",EDGE,"E81"),sQuery(id+"F6.wireOp",EDGE,"E82.MirrorCS"),sQuery(id+"F6.wireOp",EDGE,"E83"),sQuery(id+"F6.wireOp",EDGE,"E86.0"),sQuery(id+"F6.wireOp",EDGE,"E87.1")])],"isStart":false});
            var sketch = newSketch(context, id + "F19", { "sketchPlane" : qUnion([Q0])});
            skCircle(sketch, "E137", {"center": v(76, -15.6) * mm, "radius": 8 * mm});
            skCircle(sketch, "E138", {"center": v(50.7, -90.02) * mm, "radius": 8 * mm});
            skSolve(sketch);
        }
        {
            var Q0;
            Q0=makeQuery(id+"F19.imprint","IMPRINT",FACE,{"disambiguationData":[TD([[makeQuery(id+"F19.imprint","IMPRINT",EDGE,{"derivedFrom":sQuery(id+"F19.wireOp",EDGE,"E137")}),1.0]])]});
            var Q1;
            Q1=makeQuery(id+"F19.imprint","IMPRINT",FACE,{"disambiguationData":[TD([[makeQuery(id+"F19.imprint","IMPRINT",EDGE,{"derivedFrom":sQuery(id+"F19.wireOp",EDGE,"E138")}),1.0]])]});
            extrude(context, id + "F20", {"entities" : qUnion([Q0, Q1]), "operationType" : NewBodyOperationType.REMOVE, "oppositeDirection" : true, "depth" : 2.5 * mm});
        }
        {
            var Q0;
            Q0=makeQuery(id+"F13.opExtrude","CAP_FACE",FACE,{"disambiguationData":[OSD([sQuery(id+"F6.wireOp",EDGE,"E88"),sQuery(id+"F6.wireOp",EDGE,"E89"),sQuery(id+"F6.wireOp",EDGE,"E90.MirrorCS"),sQuery(id+"F6.wireOp",EDGE,"E91"),sQuery(id+"F6.wireOp",EDGE,"E98"),sQuery(id+"F6.wireOp",EDGE,"E99"),sQuery(id+"F6.wireOp",EDGE,"E100"),sQuery(id+"F6.wireOp",EDGE,"E101.filletArc"),sQuery(id+"F6.wireOp",EDGE,"E102.filletArc"),sQuery(id+"F6.wireOp",EDGE,"E103.0"),sQuery(id+"F6.wireOp",EDGE,"E103.1")])],"isStart":false});
            var sketch = newSketch(context, id + "F21", { "sketchPlane" : qUnion([Q0])});
            skCircle(sketch, "E139", {"center": v(50.75, 63.47) * mm, "radius": 8 * mm});
            skCircle(sketch, "E140", {"center": v(-29.72, 4.1) * mm, "radius": 8 * mm});
            skSolve(sketch);
        }
        {
            var Q0;
            Q0=makeQuery(id+"F21.imprint","IMPRINT",FACE,{"disambiguationData":[TD([[makeQuery(id+"F21.imprint","IMPRINT",EDGE,{"derivedFrom":sQuery(id+"F21.wireOp",EDGE,"E139")}),1.0]])]});
            var Q1;
            Q1=makeQuery(id+"F21.imprint","IMPRINT",FACE,{"disambiguationData":[TD([[makeQuery(id+"F21.imprint","IMPRINT",EDGE,{"derivedFrom":sQuery(id+"F21.wireOp",EDGE,"E140")}),1.0]])]});
            extrude(context, id + "F22", {"entities" : qUnion([Q0, Q1]), "operationType" : NewBodyOperationType.REMOVE, "oppositeDirection" : true, "depth" : 2.5 * mm});
        }
        {
            var Q0;
            Q0=makeQuery(id+"F14.opExtrude","CAP_FACE",FACE,{"disambiguationData":[OSD([sQuery(id+"F7.wireOp",EDGE,"E104.0"),sQuery(id+"F7.wireOp",EDGE,"E104.1"),sQuery(id+"F7.wireOp",EDGE,"E105"),sQuery(id+"F7.wireOp",EDGE,"E106"),sQuery(id+"F7.wireOp",EDGE,"E110"),sQuery(id+"F7.wireOp",EDGE,"E111")])],"isStart":false});
            var sketch = newSketch(context, id + "F23", { "sketchPlane" : qUnion([Q0])});
            skCircle(sketch, "E141", {"center": v(-29.72, 4.1) * mm, "radius": 8 * mm});
            skCircle(sketch, "E142", {"center": v(50.7, -90.02) * mm, "radius": 8 * mm});
            skSolve(sketch);
        }
        {
            var Q0;
            Q0=makeQuery(id+"F23.imprint","IMPRINT",FACE,{"disambiguationData":[TD([[makeQuery(id+"F23.imprint","IMPRINT",EDGE,{"derivedFrom":sQuery(id+"F23.wireOp",EDGE,"E141")}),1.0]])]});
            var Q1;
            Q1=makeQuery(id+"F23.imprint","IMPRINT",FACE,{"disambiguationData":[TD([[makeQuery(id+"F23.imprint","IMPRINT",EDGE,{"derivedFrom":sQuery(id+"F23.wireOp",EDGE,"E142")}),1.0]])]});
            extrude(context, id + "F24", {"entities" : qUnion([Q0, Q1]), "operationType" : NewBodyOperationType.REMOVE, "oppositeDirection" : true, "depth" : 2.5 * mm});
        }
        {
            var Q0;
            Q0=makeQuery(id+"F13.opExtrude","SWEPT_BODY",BODY,{"disambiguationData":[OSD([sQuery(id+"F6.wireOp",EDGE,"E72"),sQuery(id+"F6.wireOp",EDGE,"E73"),sQuery(id+"F6.wireOp",EDGE,"E77"),sQuery(id+"F6.wireOp",EDGE,"E78.MirrorCS"),sQuery(id+"F6.wireOp",EDGE,"E79.0"),sQuery(id+"F6.wireOp",EDGE,"E79.1"),sQuery(id+"F6.wireOp",EDGE,"E94"),sQuery(id+"F6.wireOp",EDGE,"E95"),sQuery(id+"F6.wireOp",EDGE,"E97.filletArc")])]});
            var Q1;
            Q1=makeQuery(id+"F13.opExtrude","SWEPT_BODY",BODY,{"disambiguationData":[OSD([sQuery(id+"F6.wireOp",EDGE,"E80"),sQuery(id+"F6.wireOp",EDGE,"E81"),sQuery(id+"F6.wireOp",EDGE,"E82.MirrorCS"),sQuery(id+"F6.wireOp",EDGE,"E83"),sQuery(id+"F6.wireOp",EDGE,"E86.0"),sQuery(id+"F6.wireOp",EDGE,"E87.1")])]});
            var Q2;
            Q2=makeQuery(id+"F13.opExtrude","SWEPT_BODY",BODY,{"disambiguationData":[OSD([sQuery(id+"F6.wireOp",EDGE,"E88"),sQuery(id+"F6.wireOp",EDGE,"E89"),sQuery(id+"F6.wireOp",EDGE,"E90.MirrorCS"),sQuery(id+"F6.wireOp",EDGE,"E91"),sQuery(id+"F6.wireOp",EDGE,"E98"),sQuery(id+"F6.wireOp",EDGE,"E99"),sQuery(id+"F6.wireOp",EDGE,"E100"),sQuery(id+"F6.wireOp",EDGE,"E101.filletArc"),sQuery(id+"F6.wireOp",EDGE,"E102.filletArc"),sQuery(id+"F6.wireOp",EDGE,"E103.0"),sQuery(id+"F6.wireOp",EDGE,"E103.1")])]});
            var Q3;
            Q3=makeQuery(id+"F14.opExtrude","SWEPT_BODY",BODY,{"disambiguationData":[OSD([sQuery(id+"F7.wireOp",EDGE,"E104.0"),sQuery(id+"F7.wireOp",EDGE,"E104.1"),sQuery(id+"F7.wireOp",EDGE,"E105"),sQuery(id+"F7.wireOp",EDGE,"E106"),sQuery(id+"F7.wireOp",EDGE,"E110"),sQuery(id+"F7.wireOp",EDGE,"E111")])]});
            var Q4;
            Q4=qCreatedBy(makeId("Right.planeOp"),FACE);
            mirror(context, id + "F25", {"entities" : qUnion([Q0, Q1, Q2, Q3]), "mirrorPlane" : qUnion([Q4])});
        }
    });
